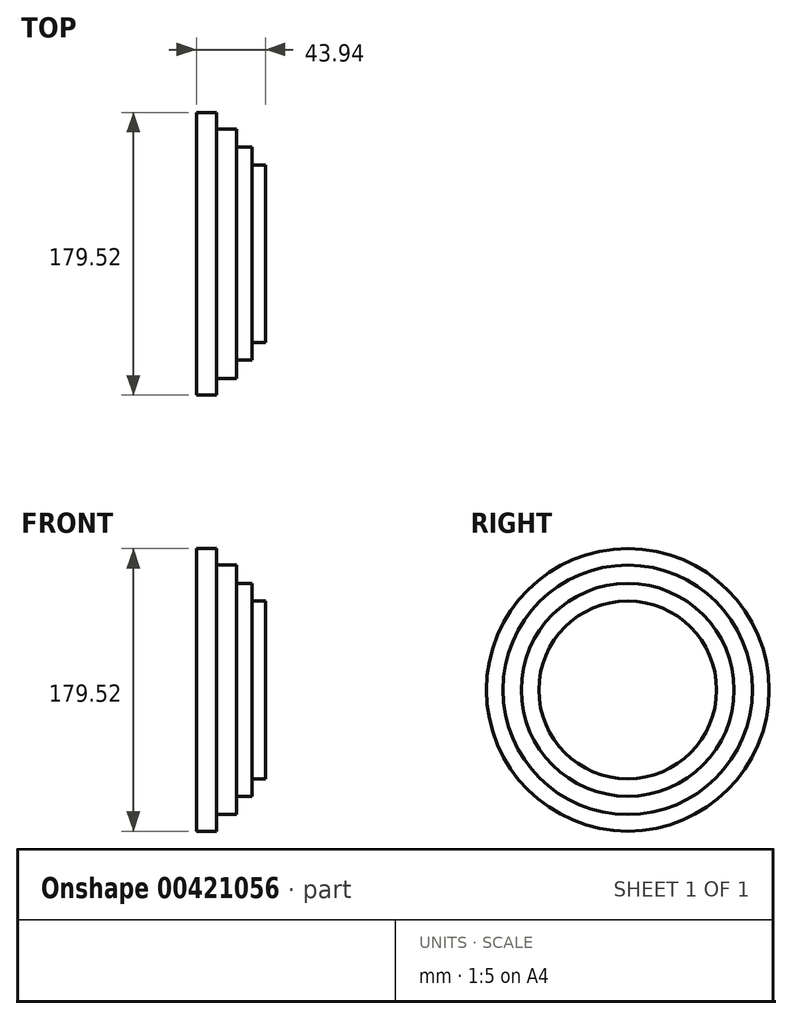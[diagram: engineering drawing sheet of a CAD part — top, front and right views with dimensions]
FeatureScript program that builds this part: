
annotation { "Feature Type Name" : "Feature", "Feature Type Description" : "" }
export const myFeature = defineFeature(function(context is Context, id is Id, definition is map)
    precondition{}
    {
        {
            var Q0;
            Q0=qCreatedBy(makeId("Right.planeOp"),FACE);
            var sketch = newSketch(context, id + "F0", { "sketchPlane" : qUnion([Q0])});
            skCircle(sketch, "E0", {"center": v(0, 0) * mm, "radius": 89.76 * mm});
            skSolve(sketch);
        }
        {
            var Q0;
            Q0=qCreatedBy(makeId("Right.planeOp"),FACE);
            var sketch = newSketch(context, id + "F1", { "sketchPlane" : qUnion([Q0])});
            skCircle(sketch, "E1", {"center": v(0, 0) * mm, "radius": 79.2 * mm});
            skSolve(sketch);
        }
        {
            var Q0;
            Q0=qCreatedBy(makeId("Right.planeOp"),FACE);
            var sketch = newSketch(context, id + "F2", { "sketchPlane" : qUnion([Q0])});
            skCircle(sketch, "E2", {"center": v(0, 0) * mm, "radius": 67.6 * mm});
            skSolve(sketch);
        }
        {
            var Q0;
            Q0=qCreatedBy(makeId("Right.planeOp"),FACE);
            var sketch = newSketch(context, id + "F3", { "sketchPlane" : qUnion([Q0])});
            skCircle(sketch, "E3", {"center": v(0, 0) * mm, "radius": 56.45 * mm});
            skSolve(sketch);
        }
        {
            var Q0;
            Q0=makeQuery(id+"F0.imprint","IMPRINT",FACE,{"disambiguationData":[TD([[makeQuery(id+"F0.imprint","IMPRINT",EDGE,{"derivedFrom":sQuery(id+"F0.wireOp",EDGE,"E0")}),1.0]])]});
            extrude(context, id + "F4", {"entities" : qUnion([Q0]), "depth" : 12.95 * mm});
        }
        {
            var Q0;
            Q0=makeQuery(id+"F1.imprint","IMPRINT",FACE,{"disambiguationData":[TD([[makeQuery(id+"F1.imprint","IMPRINT",EDGE,{"derivedFrom":sQuery(id+"F1.wireOp",EDGE,"E1")}),1.0]])]});
            extrude(context, id + "F5", {"entities" : qUnion([Q0]), "operationType" : NewBodyOperationType.ADD, "depth" : 25.4 * mm});
        }
        {
            var Q0;
            Q0=makeQuery(id+"F2.imprint","IMPRINT",FACE,{"disambiguationData":[TD([[makeQuery(id+"F2.imprint","IMPRINT",EDGE,{"derivedFrom":sQuery(id+"F2.wireOp",EDGE,"E2")}),1.0]])]});
            extrude(context, id + "F6", {"entities" : qUnion([Q0]), "operationType" : NewBodyOperationType.ADD, "depth" : 35.3 * mm});
        }
        {
            var Q0;
            Q0=makeQuery(id+"F3.imprint","IMPRINT",FACE,{"disambiguationData":[TD([[makeQuery(id+"F3.imprint","IMPRINT",EDGE,{"derivedFrom":sQuery(id+"F3.wireOp",EDGE,"E3")}),1.0]])]});
            extrude(context, id + "F7", {"entities" : qUnion([Q0]), "operationType" : NewBodyOperationType.ADD, "depth" : 43.94 * mm});
        }
    });
